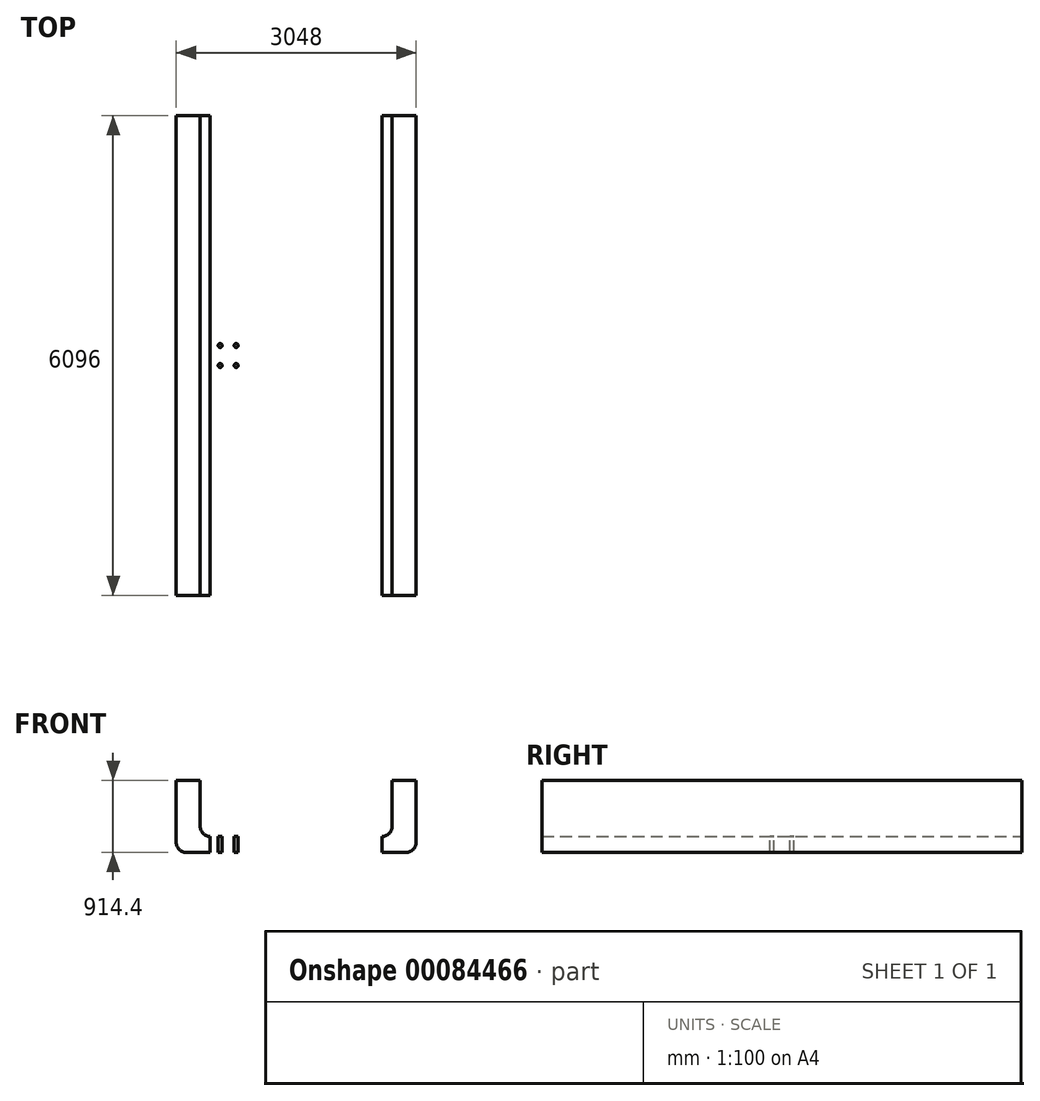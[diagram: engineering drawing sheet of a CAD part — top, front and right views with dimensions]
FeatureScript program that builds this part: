
annotation { "Feature Type Name" : "Feature", "Feature Type Description" : "" }
export const myFeature = defineFeature(function(context is Context, id is Id, definition is map)
    precondition{}
    {
        {
            var Q0;
            Q0=qCreatedBy(makeId("Front.planeOp"),FACE);
            var sketch = newSketch(context, id + "F0", { "sketchPlane" : qUnion([Q0])});
            skLineSegment(sketch, "E0", {"start": v(0, 0) * mm, "end": v(0, 1633.16) * mm, "construction": true});
            skLineSegment(sketch, "E1", {"start": v(0, 0) * mm, "end": v(-1397, 0) * mm});
            skLineSegment(sketch, "E2", {"start": v(0, 203.2) * mm, "end": v(-1092.2, 203.2) * mm});
            skLineSegment(sketch, "E3", {"start": v(-1219.2, 330.2) * mm, "end": v(-1219.2, 914.4) * mm});
            skLineSegment(sketch, "E4", {"start": v(-1219.2, 914.4) * mm, "end": v(-1524, 914.4) * mm});
            skLineSegment(sketch, "E5", {"start": v(-1524, 914.4) * mm, "end": v(-1524, 127) * mm});
            skLineSegment(sketch, "E6", {"start": v(0, 203.2) * mm, "end": v(0, 0) * mm});
            skArc(sketch, "E7", {"start": v(-1219.2, 330.2) * mm, "mid": v(-1182, 240.4) * mm, "end": v(-1092.2, 203.2) * mm});
            skArc(sketch, "E8", {"start": v(-1524, 127) * mm, "mid": v(-1486.8, 37.2) * mm, "end": v(-1397, 0) * mm});
            skLineSegment(sketch, "E9.MirrorCS", {"start": v(0, 203.2) * mm, "end": v(1092.2, 203.2) * mm});
            skArc(sketch, "E10.MirrorCS", {"start": v(1219.2, 330.2) * mm, "mid": v(1182, 240.4) * mm, "end": v(1092.2, 203.2) * mm});
            skLineSegment(sketch, "E11.MirrorCS", {"start": v(1219.2, 330.2) * mm, "end": v(1219.2, 914.4) * mm});
            skLineSegment(sketch, "E12.MirrorCS", {"start": v(1219.2, 914.4) * mm, "end": v(1524, 914.4) * mm});
            skLineSegment(sketch, "E13.MirrorCS", {"start": v(1524, 914.4) * mm, "end": v(1524, 127) * mm});
            skArc(sketch, "E14.MirrorCS", {"start": v(1524, 127) * mm, "mid": v(1486.8, 37.2) * mm, "end": v(1397, 0) * mm});
            skLineSegment(sketch, "E15.MirrorCS", {"start": v(0, 0) * mm, "end": v(1397, 0) * mm});
            skSolve(sketch);
        }
        {
            var Q0;
            Q0=makeQuery(id+"F0.imprint","IMPRINT",FACE,{"disambiguationData":[TD([[makeQuery(id+"F0.imprint","IMPRINT",EDGE,{"derivedFrom":sQuery(id+"F0.wireOp",EDGE,"E1")}),-1.0]])]});
            var Q1;
            Q1=makeQuery(id+"F0.imprint","IMPRINT",FACE,{"disambiguationData":[TD([[makeQuery(id+"F0.imprint","IMPRINT",EDGE,{"derivedFrom":sQuery(id+"F0.wireOp",EDGE,"E6")}),1.0]])]});
            extrude(context, id + "F1", {"entities" : qUnion([Q0, Q1]), "endBound" : BoundingType.SYMMETRIC, "depth" : 6096 * mm});
        }
        {
            var Q0;
            Q0=makeQuery(id+"F1.opExtrude","SWEPT_FACE",FACE,{"disambiguationData":[OSD([sQuery(id+"F0.wireOp",EDGE,"E2"),sQuery(id+"F0.wireOp",EDGE,"E9.MirrorCS")])]});
            var sketch = newSketch(context, id + "F2", { "sketchPlane" : qUnion([Q0])});
            skLineSegment(sketch, "E16.0", {"start": v(1092.2, -3048) * mm, "end": v(1092.2, 3048) * mm});
            skLineSegment(sketch, "E16.1", {"start": v(-1092.2, -3048) * mm, "end": v(-1092.2, 3048) * mm});
            skLineSegment(sketch, "E16.2", {"start": v(-1219.2, -3048) * mm, "end": v(-1219.2, 3048) * mm});
            skLineSegment(sketch, "E16.3", {"start": v(-1524, -3048) * mm, "end": v(-1524, 3048) * mm});
            skLineSegment(sketch, "E16.4", {"start": v(1524, -3048) * mm, "end": v(1524, 3048) * mm});
            skLineSegment(sketch, "E16.5", {"start": v(1219.2, -3048) * mm, "end": v(1219.2, 3048) * mm});
            skLineSegment(sketch, "E17", {"start": v(1092.2, 3048) * mm, "end": v(-1092.2, -3048) * mm, "construction": true});
            skLineSegment(sketch, "E18", {"start": v(-1092.2, 3048) * mm, "end": v(1092.2, -3048) * mm, "construction": true});
            skLineSegment(sketch, "E19", {"start": v(0, -3048) * mm, "end": v(0, 3048) * mm, "construction": true});
            skLineSegment(sketch, "E20", {"start": v(-1524, 0) * mm, "end": v(1524, 0) * mm, "construction": true});
            skCircle(sketch, "E21", {"center": v(762, 127) * mm, "radius": 25.4 * mm});
            skCircle(sketch, "E22", {"center": v(965.2, 127) * mm, "radius": 25.4 * mm});
            skCircle(sketch, "E23", {"center": v(762, -127) * mm, "radius": 25.4 * mm});
            skCircle(sketch, "E24", {"center": v(965.2, -127) * mm, "radius": 25.4 * mm});
            skCircle(sketch, "E25.MirrorC", {"center": v(-762, 127) * mm, "radius": 25.4 * mm});
            skCircle(sketch, "E26.MirrorC", {"center": v(-965.2, 127) * mm, "radius": 25.4 * mm});
            skCircle(sketch, "E27.MirrorC", {"center": v(-762, -127) * mm, "radius": 25.4 * mm});
            skCircle(sketch, "E28.MirrorC", {"center": v(-965.2, -127) * mm, "radius": 25.4 * mm});
            skSolve(sketch);
        }
        {
            var Q0;
            Q0=makeQuery(id+"F2.imprint","IMPRINT",FACE,{"disambiguationData":[TD([[makeQuery(id+"F2.imprint","IMPRINT",EDGE,{"derivedFrom":sQuery(id+"F2.wireOp",EDGE,"E26.MirrorC")}),-1.0]])]});
            var Q1;
            Q1=makeQuery(id+"F2.imprint","IMPRINT",FACE,{"disambiguationData":[TD([[makeQuery(id+"F2.imprint","IMPRINT",EDGE,{"derivedFrom":sQuery(id+"F2.wireOp",EDGE,"E25.MirrorC")}),-1.0]])]});
            var Q2;
            Q2=makeQuery(id+"F2.imprint","IMPRINT",FACE,{"disambiguationData":[TD([[makeQuery(id+"F2.imprint","IMPRINT",EDGE,{"derivedFrom":sQuery(id+"F2.wireOp",EDGE,"E28.MirrorC")}),-1.0]])]});
            var Q3;
            Q3=makeQuery(id+"F2.imprint","IMPRINT",FACE,{"disambiguationData":[TD([[makeQuery(id+"F2.imprint","IMPRINT",EDGE,{"derivedFrom":sQuery(id+"F2.wireOp",EDGE,"E27.MirrorC")}),-1.0]])]});
            var Q4;
            Q4=makeQuery(id+"F2.imprint","IMPRINT",FACE,{"disambiguationData":[TD([[makeQuery(id+"F2.imprint","IMPRINT",EDGE,{"derivedFrom":sQuery(id+"F2.wireOp",EDGE,"E21")}),1.0]])]});
            var Q5;
            Q5=makeQuery(id+"F2.imprint","IMPRINT",FACE,{"disambiguationData":[TD([[makeQuery(id+"F2.imprint","IMPRINT",EDGE,{"derivedFrom":sQuery(id+"F2.wireOp",EDGE,"E22")}),1.0]])]});
            var Q6;
            Q6=makeQuery(id+"F2.imprint","IMPRINT",FACE,{"disambiguationData":[TD([[makeQuery(id+"F2.imprint","IMPRINT",EDGE,{"derivedFrom":sQuery(id+"F2.wireOp",EDGE,"E24")}),1.0]])]});
            var Q7;
            Q7=makeQuery(id+"F2.imprint","IMPRINT",FACE,{"disambiguationData":[TD([[makeQuery(id+"F2.imprint","IMPRINT",EDGE,{"derivedFrom":sQuery(id+"F2.wireOp",EDGE,"E23")}),1.0]])]});
            extrude(context, id + "F3", {"entities" : qUnion([Q0, Q1, Q2, Q3, Q4, Q5, Q6, Q7]), "operationType" : NewBodyOperationType.REMOVE, "endBound" : BoundingType.THROUGH_ALL, "oppositeDirection" : true, "depth" : 25.4 * mm});
        }
    });
